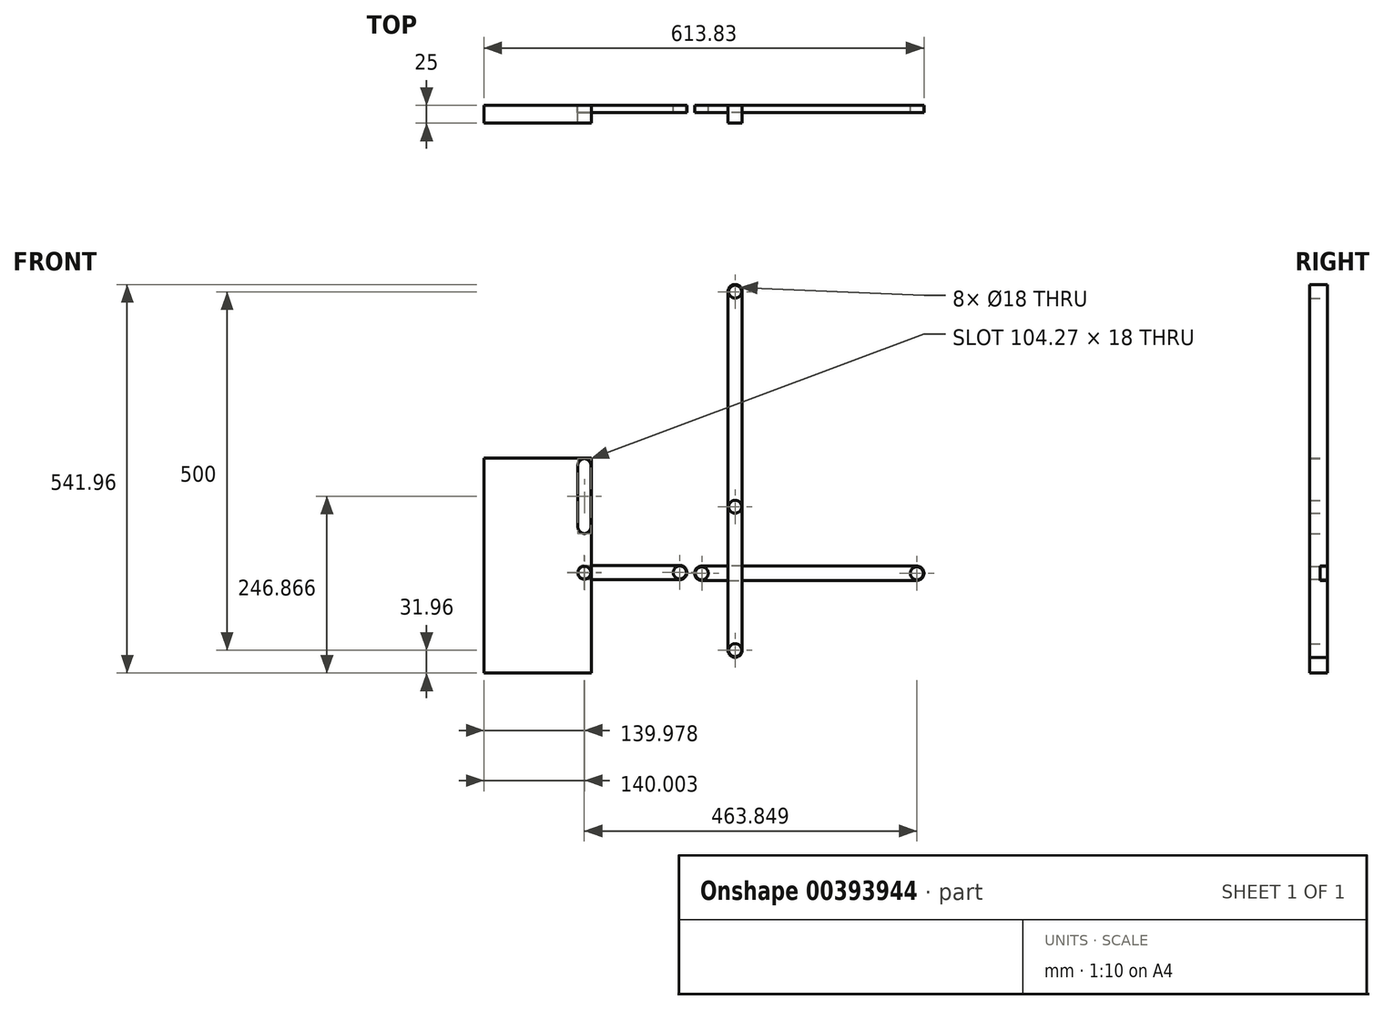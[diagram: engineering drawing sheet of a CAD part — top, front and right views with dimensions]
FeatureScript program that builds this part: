
annotation { "Feature Type Name" : "Feature", "Feature Type Description" : "" }
export const myFeature = defineFeature(function(context is Context, id is Id, definition is map)
    precondition{}
    {
        {
            var Q0;
            Q0=qCreatedBy(makeId("Front.planeOp"),FACE);
            var sketch = newSketch(context, id + "F0", { "sketchPlane" : qUnion([Q0])});
            skLineSegment(sketch, "E0.bottom", {"start": v(-10, 500) * mm, "end": v(10, 500) * mm, "construction": true});
            skLineSegment(sketch, "E0.left", {"start": v(10, 500) * mm, "end": v(10, 0) * mm});
            skLineSegment(sketch, "E0.right", {"start": v(-10, 500) * mm, "end": v(-10, 0) * mm});
            skLineSegment(sketch, "E1", {"start": v(0, 0) * mm, "end": v(0, 500) * mm, "construction": true});
            skArc(sketch, "E2", {"start": v(10, 0) * mm, "mid": v(0, -10) * mm, "end": v(-10, 0) * mm});
            skCircle(sketch, "E3.0", {"center": v(0, 0) * mm, "radius": 9 * mm});
            skLineSegment(sketch, "E4", {"start": v(-10, 0) * mm, "end": v(10, 0) * mm, "construction": true});
            skArc(sketch, "E5", {"start": v(10, 500) * mm, "mid": v(0, 510) * mm, "end": v(-10, 500) * mm});
            skCircle(sketch, "E6.0", {"center": v(0, 500) * mm, "radius": 9 * mm});
            skCircle(sketch, "E7", {"center": v(0, 200) * mm, "radius": 9 * mm});
            skSolve(sketch);
        }
        {
            var Q0;
            Q0=makeQuery(id+"F0.imprint","IMPRINT",FACE,{"disambiguationData":[TD([[makeQuery(id+"F0.imprint","IMPRINT",EDGE,{"derivedFrom":sQuery(id+"F0.wireOp",EDGE,"E0.left")}),-1.0]])]});
            extrude(context, id + "F1", {"entities" : qUnion([Q0]), "depth" : 25 * mm});
        }
        {
            var Q0;
            Q0=qCreatedBy(makeId("Front.planeOp"),FACE);
            var sketch = newSketch(context, id + "F2", { "sketchPlane" : qUnion([Q0])});
            skCircle(sketch, "E8", {"center": v(0, 0) * mm, "radius": 9 * mm});
            skCircle(sketch, "E9", {"center": v(0, 0) * mm, "radius": 10 * mm});
            skLineSegment(sketch, "E10", {"start": v(0, 0) * mm, "end": v(-200.28, 106.86) * mm, "construction": true});
            skLineSegment(sketch, "E11", {"start": v(-200.28, 268.04) * mm, "end": v(-200.28, -31.96) * mm});
            skLineSegment(sketch, "E12", {"start": v(-200.28, -31.96) * mm, "end": v(-350.28, -31.96) * mm});
            skLineSegment(sketch, "E13", {"start": v(-350.28, -31.96) * mm, "end": v(-350.28, 268.04) * mm});
            skLineSegment(sketch, "E14", {"start": v(-350.28, 268.04) * mm, "end": v(-200.28, 268.04) * mm});
            skCircle(sketch, "E15", {"center": v(-210.28, 258.04) * mm, "radius": 10 * mm, "construction": true});
            skArc(sketch, "E16", {"start": v(-201.28, 258.04) * mm, "mid": v(-210.28, 267.04) * mm, "end": v(-219.28, 258.04) * mm});
            skCircle(sketch, "E17", {"center": v(-210.28, 108.04) * mm, "radius": 10 * mm, "construction": true});
            skCircle(sketch, "E18", {"center": v(-210.28, 108.04) * mm, "radius": 9 * mm});
            skLineSegment(sketch, "E19", {"start": v(-210.28, 258.04) * mm, "end": v(-210.28, 171.77) * mm, "construction": true});
            skArc(sketch, "E20", {"start": v(-219.28, 171.77) * mm, "mid": v(-210.28, 162.77) * mm, "end": v(-201.28, 171.77) * mm});
            skLineSegment(sketch, "E21", {"start": v(-219.28, 171.77) * mm, "end": v(-219.28, 258.04) * mm});
            skLineSegment(sketch, "E22", {"start": v(-201.28, 258.04) * mm, "end": v(-201.28, 171.77) * mm});
            skSolve(sketch);
        }
        {
            var Q0;
            Q0=makeQuery(id+"F2.imprint","IMPRINT",FACE,{"disambiguationData":[TD([[makeQuery(id+"F2.imprint","IMPRINT",EDGE,{"derivedFrom":sQuery(id+"F2.wireOp",EDGE,"E11")}),-1.0]])]});
            extrude(context, id + "F3", {"entities" : qUnion([Q0]), "depth" : 25 * mm});
        }
        {
            var Q0;
            Q0=qCreatedBy(makeId("Front.planeOp"),FACE);
            var sketch = newSketch(context, id + "F4", { "sketchPlane" : qUnion([Q0])});
            skPoint(sketch, "E23", {"position": v(0, 0) * mm});
            skLineSegment(sketch, "E24", {"start": v(0, 0) * mm, "end": v(-77.22, 108.38) * mm, "construction": true});
            skLineSegment(sketch, "E25", {"start": v(-77.22, 108.38) * mm, "end": v(-210.3, 108.38) * mm, "construction": true});
            skArc(sketch, "E26", {"start": v(-210.3, 118.38) * mm, "mid": v(-220.3, 108.38) * mm, "end": v(-210.3, 98.38) * mm});
            skCircle(sketch, "E27", {"center": v(-210.3, 108.38) * mm, "radius": 9 * mm});
            skCircle(sketch, "E28", {"center": v(-77.22, 108.38) * mm, "radius": 9 * mm});
            skArc(sketch, "E29", {"start": v(-77.22, 98.38) * mm, "mid": v(-67.22, 108.38) * mm, "end": v(-77.22, 118.38) * mm});
            skLineSegment(sketch, "E30", {"start": v(-210.3, 118.38) * mm, "end": v(-77.22, 118.38) * mm});
            skLineSegment(sketch, "E31", {"start": v(-77.22, 98.38) * mm, "end": v(-210.3, 98.38) * mm});
            skSolve(sketch);
        }
        {
            var Q0;
            Q0=makeQuery(id+"F4.imprint","IMPRINT",FACE,{"disambiguationData":[TD([[makeQuery(id+"F4.imprint","IMPRINT",EDGE,{"derivedFrom":sQuery(id+"F4.wireOp",EDGE,"E26")}),1.0]])]});
            extrude(context, id + "F5", {"entities" : qUnion([Q0]), "depth" : 10 * mm});
        }
        {
            var Q0;
            Q0=qCreatedBy(makeId("Front.planeOp"),FACE);
            var sketch = newSketch(context, id + "F6", { "sketchPlane" : qUnion([Q0])});
            skCircle(sketch, "E32", {"center": v(-46.45, 107.24) * mm, "radius": 9 * mm});
            skArc(sketch, "E33", {"start": v(-46.45, 117.24) * mm, "mid": v(-56.45, 107.22) * mm, "end": v(-46.42, 97.24) * mm});
            skLineSegment(sketch, "E34", {"start": v(-46.45, 107.24) * mm, "end": v(253.55, 107.24) * mm, "construction": true});
            skArc(sketch, "E35", {"start": v(253.55, 97.24) * mm, "mid": v(263.55, 107.24) * mm, "end": v(253.55, 117.24) * mm});
            skCircle(sketch, "E36", {"center": v(253.55, 107.24) * mm, "radius": 9 * mm});
            skLineSegment(sketch, "E37", {"start": v(253.55, 117.24) * mm, "end": v(-46.45, 117.24) * mm});
            skLineSegment(sketch, "E38", {"start": v(-46.42, 97.24) * mm, "end": v(253.55, 97.24) * mm});
            skSolve(sketch);
        }
        {
            var Q0;
            Q0=makeQuery(id+"F6.imprint","IMPRINT",FACE,{"disambiguationData":[TD([[makeQuery(id+"F6.imprint","IMPRINT",EDGE,{"derivedFrom":sQuery(id+"F6.wireOp",EDGE,"E32")}),-1.0]])]});
            extrude(context, id + "F7", {"entities" : qUnion([Q0]), "depth" : 10 * mm});
        }
    });
